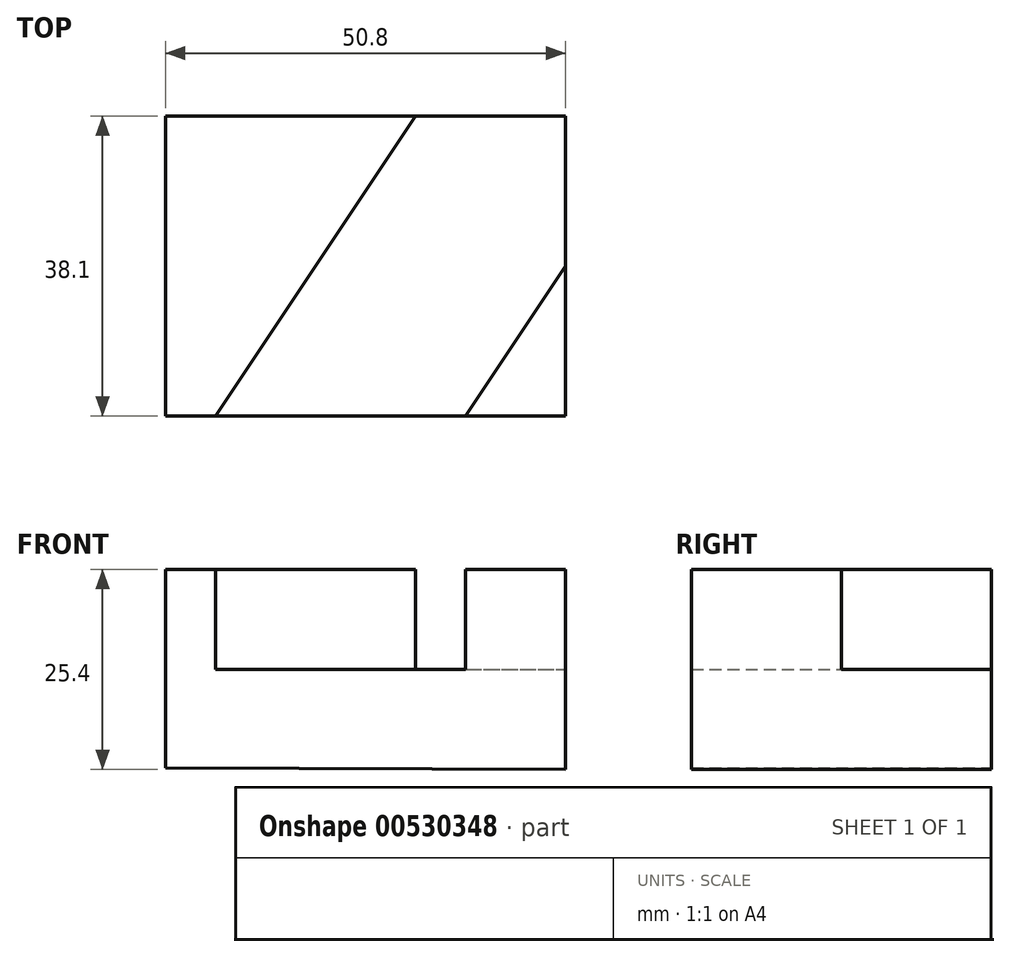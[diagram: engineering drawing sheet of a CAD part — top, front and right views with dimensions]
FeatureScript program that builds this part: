
annotation { "Feature Type Name" : "Feature", "Feature Type Description" : "" }
export const myFeature = defineFeature(function(context is Context, id is Id, definition is map)
    precondition{}
    {
        {
            var Q0;
            Q0=qCreatedBy(makeId("Front.planeOp"),FACE);
            var sketch = newSketch(context, id + "F0", { "sketchPlane" : qUnion([Q0])});
            skLineSegment(sketch, "E0", {"start": v(-43.86, 16.54) * mm, "end": v(-43.86, 41.73) * mm});
            skLineSegment(sketch, "E1", {"start": v(-43.86, 41.73) * mm, "end": v(6.94, 41.73) * mm});
            skLineSegment(sketch, "E2", {"start": v(6.94, 41.73) * mm, "end": v(6.94, 16.33) * mm});
            skLineSegment(sketch, "E3", {"start": v(6.94, 16.33) * mm, "end": v(-43.86, 16.54) * mm});
            skSolve(sketch);
        }
        {
            var Q0;
            Q0 = qSketchRegion(id + "F0", true);
            extrude(context, id + "F1", {"entities" : qUnion([Q0]), "depth" : 38.1 * mm, "offsetDistance" : 25.4 * mm});
        }
        {
            var Q0;
            Q0=makeQuery(id+"F1.opExtrude","SWEPT_FACE",FACE,{"disambiguationData":[OSD([sQuery(id+"F0.wireOp",EDGE,"E1")])]});
            var sketch = newSketch(context, id + "F2", { "sketchPlane" : qUnion([Q0])});
            skLineSegment(sketch, "E4", {"start": v(-37.5, -38.1) * mm, "end": v(-12.11, 0) * mm});
            skSolve(sketch);
        }
        {
            var Q0;
            Q0 = qSketchRegion(id + "F2", true);
            var Q1;
            {var subQ0=sQuery(id+"F2.wireOp",EDGE,"E4");Q1=makeQuery(id+"F2.imprint","IMPRINT",FACE,{"disambiguationData":[TD([[makeQuery(id+"F2.imprint","IMPRINT",EDGE,{"derivedFrom":subQ0}),-1.0]])]});}
            extrude(context, id + "F3", {"entities" : qUnion([Q0, Q1]), "operationType" : NewBodyOperationType.REMOVE, "oppositeDirection" : true, "depth" : 12.7 * mm, "offsetDistance" : 25.4 * mm});
        }
        {
            var Q0;
            Q0=makeQuery(id+"F3.boolean.opBoolean","COPY",FACE,{"derivedFrom":makeQuery(id+"F3.opExtrude","CAP_FACE",FACE,{"disambiguationData":[OSD([sQuery(id+"F0.wireOp",EDGE,"E1"),sQuery(id+"F0.wireOp",EDGE,"E2"),sQuery(id+"F2.wireOp",EDGE,"E4")])],"isStart":false})});
            var sketch = newSketch(context, id + "F4", { "sketchPlane" : qUnion([Q0])});
            skLineSegment(sketch, "E5", {"start": v(-5.76, -38.1) * mm, "end": v(6.94, -19.05) * mm});
            skSolve(sketch);
        }
        {
            var Q0;
            Q0 = qSketchRegion(id + "F4", true);
            var Q1;
            {var subQ0=sQuery(id+"F4.wireOp",EDGE,"E5");Q1=makeQuery(id+"F4.imprint","IMPRINT",FACE,{"disambiguationData":[TD([[makeQuery(id+"F4.imprint","IMPRINT",EDGE,{"derivedFrom":subQ0}),-1.0]])]});}
            extrude(context, id + "F5", {"entities" : qUnion([Q0, Q1]), "operationType" : NewBodyOperationType.ADD, "depth" : 12.7 * mm, "offsetDistance" : 25.4 * mm});
        }
    });
